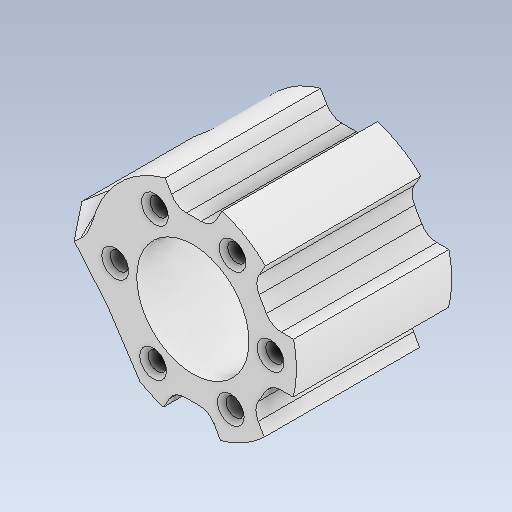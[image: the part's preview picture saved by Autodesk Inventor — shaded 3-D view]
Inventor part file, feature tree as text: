
AUTODESK INVENTOR PART (.ipt)
format: ipt  version: 2020 (Build 240168000, 168)  size: 410,112 bytes
history: native  units: mm
features: sketch x7, extrude x6, reference x6, projected_geometry x5, chamfer x3, other x3, plane x2, fillet x2, shell x2, hole x1, pattern_circular x1
ambient origin geometry x8: Origin, YZ Plane, XZ Plane, XY Plane, X Axis, Y Axis, Z Axis, Center Point
bodies: Solid1 (feature_tree)
feature tree (38):
  sketch  "Sketch1"  dims[d0=26.0mm d1=48.0mm]
  plane  "Work Plane1"
  extrude  "Extrusion1"  Depth=48.0mm
  hole  "Hole1"  [1 undecoded]
  chamfer  "Chamfer1"  Distance=50.0mm
  extrude  "Extrusion2"  Depth=2.0mm TaperAngle=45.0deg
  sketch  "Sketch4"  dims[d14=2.0mm d15=50.0mm d16=0.0mm]
  plane  "Work Plane2"
  extrude  "Extrusion3"  Depth=10.0mm
  chamfer  "Chamfer2"  Distance=10.0mm
  extrude  "Extrusion4"  Depth=2.0mm
  extrude  "Extrusion5"  Depth=2.0mm
  extrude  "Extrusion6"  Depth=2.0mm
  pattern_circular  "Circular Pattern1"  Angle=120.0deg  [1 undecoded]
  fillet  "Fillet1"  [1 undecoded]
  fillet  "Fillet2"  Radius=50.0mm
  chamfer  "Chamfer3"  Distance=40.0mm Angle=180.0deg
  reference  "Reference1"
  sketch  "Sketch2"  dims[d2=10.0mm d3=0.0mm]
  projected_geometry  "Projected Loop1"
  sketch  "Sketch3"  dims[d4=4.2mm d5=6.0mm d6=4.0mm d7=2.0mm d8=90.0deg d9=8.0mm d10=20.594885mm d11=1.0mm d12=2.0mm d13=45.0deg]
  reference  "Reference2"
  projected_geometry  "Projected Loop2"
  projected_geometry  "Projected Loop3"
  reference  "Reference3"
  reference  "Reference4"
  reference  "Reference5"
  sketch  "Sketch5"  dims[d17=50.0mm d18=0.0mm d19=5.0mm d20=2.0mm d21=45.0deg]
  reference  "Reference6"
  sketch  "Sketch6"  dims[d22=4.0mm d23=4.0mm d24=10.0mm d25=0.0mm]
  projected_geometry  "Projected Loop4"
  sketch  "Sketch7"  dims[d26=50.0mm d27=0.0mm d28=3.0mm d29=4.0mm d30=4.0mm d31=120.0deg d32=120.0deg d33=50.0mm d34=0.0mm d35=40.0mm d36=180.0deg d38=4.0mm d39=4.0mm d40=1.0mm d41=2.0mm d42=45.0deg]
  projected_geometry  "Projected Loop5"
  parser-record x1  (decoder bookkeeping rows leaked as tree rows — omitted from the tree; the rows remain in map.json)
  other  "reducer_3.iam"
  other  "motor_h_3_m:1"
  shell  "shell_3:1"  Thickness=4.0mm
  shell  "shell_4:1"  Thickness=4.0mm
note: 3 required parameter values undecoded (feature->parameter linkage not recoverable at this tier; creation-order binding heuristic only, values carry confidence <= 0.55)
note: 1 file-system path scrubbed to <path> (originals preserved in map.json)
